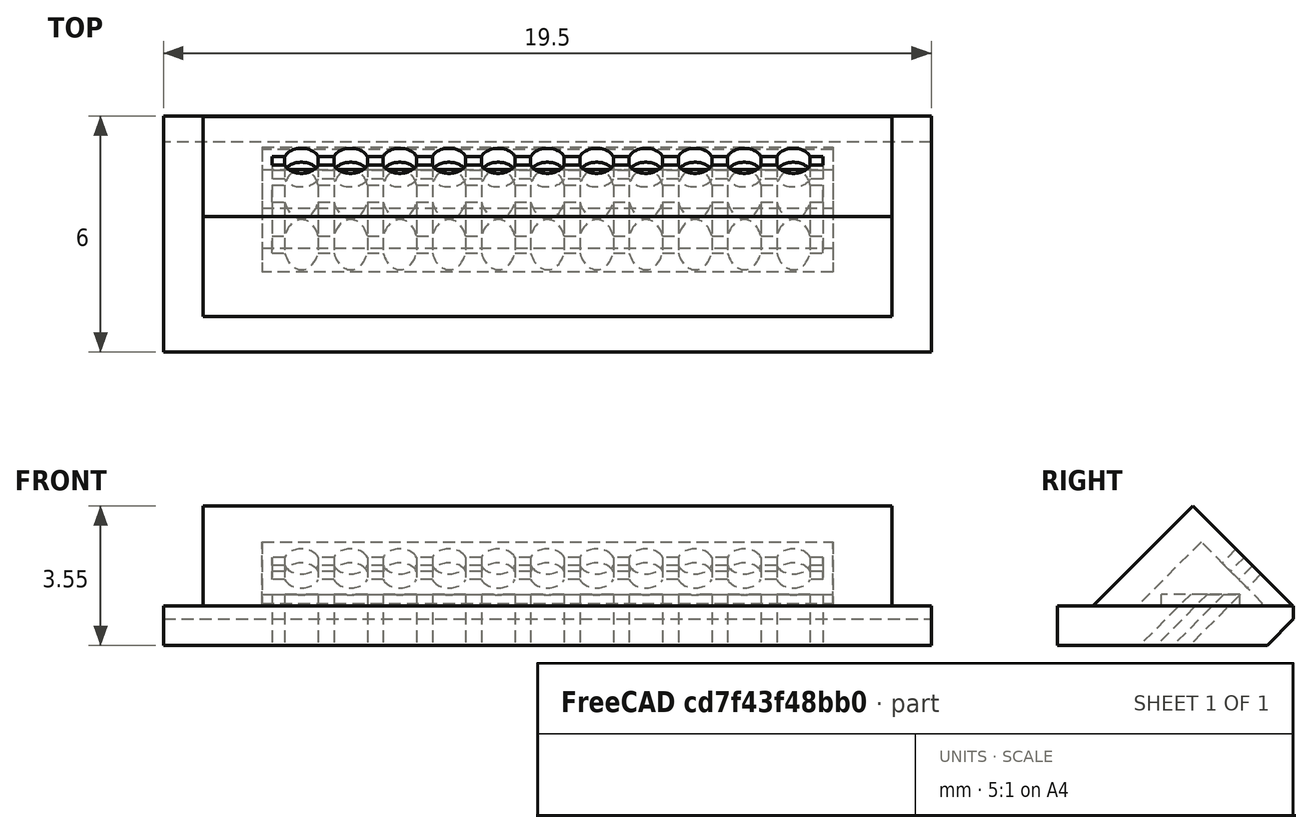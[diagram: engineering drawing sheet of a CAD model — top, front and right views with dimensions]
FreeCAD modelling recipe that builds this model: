
FCSTD DOCUMENT  (FreeCAD 0.18.4R)
Label: CableGasket3
License: All rights reserved
LicenseURL: http://en.wikipedia.org/wiki/All_rights_reserved
objects: Part::Cylinder×22, Part::Box×8, Part::Cut×5, Part::MultiFuse×4, Mesh::Feature×1
note: 39 computed .brp shape members not serialized (recipe doc carries the construction recipe); baked Part::Feature solids carry a one-line shape summary decoded from their .brp

FEATURE [Part::Box] Box001  label="Würfel001"
  AttacherType = Attacher::AttachEngine3D
  Height = 10
  Length = 17.5
  Placement = pos=(-7.5,-2,0) rot=(0,0,1;0rad)
  Width = 4
FEATURE [Part::Box] Box002  label="Würfel002"
  AttacherType = Attacher::AttachEngine3D
  Height = 10
  Length = 20
  Placement = pos=(-10,-3,-0.4) rot=(1,0,0;0.785398rad)
  Width = 14.5
FEATURE [Part::Box] Box003  label="Würfel003"
  AttacherType = Attacher::AttachEngine3D
  Height = 6
  Length = 19.5
  Placement = pos=(-8.5,-2.31,1.7) rot=(-1,0,0;0.785398rad)
  Width = 1
FEATURE [Part::Cylinder] Cylinder009  label="Draht010"
  Angle = 360
  AttacherType = Attacher::AttachEngine3D
  Height = 10
  Radius = 0.45
FEATURE [Part::Cylinder] Cylinder010  label="Draht011"
  Angle = 360
  AttacherType = Attacher::AttachEngine3D
  Height = 10
  Placement = pos=(1.25,0,0) rot=(0,0,1;0rad)
  Radius = 0.45
FEATURE [Part::Cylinder] Cylinder011  label="Draht012"
  Angle = 360
  AttacherType = Attacher::AttachEngine3D
  Height = 10
  Placement = pos=(2.5,0,0) rot=(0,0,1;0rad)
  Radius = 0.45
FEATURE [Part::Cylinder] Cylinder012  label="Draht013"
  Angle = 360
  AttacherType = Attacher::AttachEngine3D
  Height = 10
  Placement = pos=(3.75,0,0) rot=(0,0,1;0rad)
  Radius = 0.45
FEATURE [Part::Cylinder] Cylinder013  label="Draht014"
  Angle = 360
  AttacherType = Attacher::AttachEngine3D
  Height = 10
  Placement = pos=(5,0,0) rot=(0,0,1;0rad)
  Radius = 0.45
FEATURE [Part::Cylinder] Cylinder014  label="Draht015"
  Angle = 360
  AttacherType = Attacher::AttachEngine3D
  Height = 10
  Placement = pos=(-1.25,0,0) rot=(0,0,1;0rad)
  Radius = 0.45
FEATURE [Part::Cylinder] Cylinder015  label="Draht016"
  Angle = 360
  AttacherType = Attacher::AttachEngine3D
  Height = 10
  Placement = pos=(-2.5,0,0) rot=(0,0,1;0rad)
  Radius = 0.45
FEATURE [Part::Cylinder] Cylinder016  label="Draht017"
  Angle = 360
  AttacherType = Attacher::AttachEngine3D
  Height = 10
  Placement = pos=(-3.75,0,0) rot=(0,0,1;0rad)
  Radius = 0.45
FEATURE [Part::Cylinder] Cylinder017  label="Draht018"
  Angle = 360
  AttacherType = Attacher::AttachEngine3D
  Height = 10
  Placement = pos=(-5,0,0) rot=(0,0,1;0rad)
  Radius = 0.45
FEATURE [Part::Box] Box004  label="Würfel004"
  AttacherType = Attacher::AttachEngine3D
  Height = 10
  Length = 14
  Placement = pos=(-5.75,-0.15,0) rot=(0,0,1;0rad)
  Width = 0.3
FEATURE [Part::Box] Box005  label="Würfel005"
  AttacherType = Attacher::AttachEngine3D
  Height = 10
  Length = 14.5
  Placement = pos=(-6,-1,0.5) rot=(0,0,1;0rad)
  Width = 2.2
FEATURE [Part::Cut] Cut
  Base = -> Box001
  Placement = pos=(0,0,1) rot=(0,0,1;0rad)
  Tool = -> Box005
FEATURE [Part::Cut] Cut001
  Base = -> Cut
  Tool = -> Box002
FEATURE [Part::Box] Box006  label="Würfel006"
  AttacherType = Attacher::AttachEngine3D
  Height = 2
  Length = 14.5
  Placement = pos=(-6,-1,2.31) rot=(-1,0,0;0.785398rad)
  Width = 0.8
FEATURE [Part::Cylinder] Cylinder018  label="Draht019"
  Angle = 360
  AttacherType = Attacher::AttachEngine3D
  Height = 10
  Placement = pos=(6.25,0,0) rot=(0,0,1;0rad)
  Radius = 0.45
FEATURE [Part::Cylinder] Cylinder019  label="Draht020"
  Angle = 360
  AttacherType = Attacher::AttachEngine3D
  Height = 10
  Placement = pos=(7.5,0,0) rot=(0,0,1;0rad)
  Radius = 0.45
FEATURE [Part::MultiFuse] Fusion001
  Shapes = -> [Cylinder019,Cylinder009,Cylinder010,Cylinder011,Cylinder012,Cylinder013,Cylinder014,Cylinder015,Cylinder016,Cylinder017,Box004,Cylinder018]
FEATURE [Part::MultiFuse] Fusion002
  Shapes = -> [Box003,Box006]
FEATURE [Part::Cut] Cut003
  Base = -> Fusion002
  Tool = -> Fusion001
FEATURE [Part::Cylinder] Cylinder020  label="Draht021"
  Angle = 360
  AttacherType = Attacher::AttachEngine3D
  Height = 10
  Radius = 0.45
FEATURE [Part::Cylinder] Cylinder021  label="Draht022"
  Angle = 360
  AttacherType = Attacher::AttachEngine3D
  Height = 10
  Placement = pos=(1.25,0,0) rot=(0,0,1;0rad)
  Radius = 0.45
FEATURE [Part::Cylinder] Cylinder022  label="Draht023"
  Angle = 360
  AttacherType = Attacher::AttachEngine3D
  Height = 10
  Placement = pos=(2.5,0,0) rot=(0,0,1;0rad)
  Radius = 0.45
FEATURE [Part::Cylinder] Cylinder023  label="Draht024"
  Angle = 360
  AttacherType = Attacher::AttachEngine3D
  Height = 10
  Placement = pos=(3.75,0,0) rot=(0,0,1;0rad)
  Radius = 0.45
FEATURE [Part::Cylinder] Cylinder024  label="Draht025"
  Angle = 360
  AttacherType = Attacher::AttachEngine3D
  Height = 10
  Placement = pos=(5,0,0) rot=(0,0,1;0rad)
  Radius = 0.45
FEATURE [Part::Cylinder] Cylinder025  label="Draht026"
  Angle = 360
  AttacherType = Attacher::AttachEngine3D
  Height = 10
  Placement = pos=(-1.25,0,0) rot=(0,0,1;0rad)
  Radius = 0.45
FEATURE [Part::Cylinder] Cylinder026  label="Draht027"
  Angle = 360
  AttacherType = Attacher::AttachEngine3D
  Height = 10
  Placement = pos=(-2.5,0,0) rot=(0,0,1;0rad)
  Radius = 0.45
FEATURE [Part::Cylinder] Cylinder027  label="Draht028"
  Angle = 360
  AttacherType = Attacher::AttachEngine3D
  Height = 10
  Placement = pos=(-3.75,0,0) rot=(0,0,1;0rad)
  Radius = 0.45
FEATURE [Part::Cylinder] Cylinder028  label="Draht029"
  Angle = 360
  AttacherType = Attacher::AttachEngine3D
  Height = 10
  Placement = pos=(-5,0,0) rot=(0,0,1;0rad)
  Radius = 0.45
FEATURE [Part::Box] Box007  label="Würfel007"
  AttacherType = Attacher::AttachEngine3D
  Height = 10
  Length = 14
  Placement = pos=(-5.75,-0.15,0) rot=(0,0,1;0rad)
  Width = 0.3
FEATURE [Part::Cylinder] Cylinder029  label="Draht030"
  Angle = 360
  AttacherType = Attacher::AttachEngine3D
  Height = 10
  Placement = pos=(7.5,0,0) rot=(0,0,1;0rad)
  Radius = 0.45
FEATURE [Part::Cylinder] Cylinder030  label="Draht031"
  Angle = 360
  AttacherType = Attacher::AttachEngine3D
  Height = 10
  Placement = pos=(6.25,0,0) rot=(0,0,1;0rad)
  Radius = 0.45
FEATURE [Part::MultiFuse] Fusion003
  Shapes = -> [Cylinder029,Cylinder020,Cylinder021,Cylinder022,Cylinder023,Cylinder024,Cylinder025,Cylinder026,Cylinder027,Cylinder028,Box007,Cylinder030]
FEATURE [Part::Cut] Cut004
  Base = -> Cut001
  Tool = -> Fusion003
FEATURE [Part::MultiFuse] Fusion
  Placement = pos=(0,0,0) rot=(1,0,0;2.35619rad)
  Shapes = -> [Cut004,Cut003]
FEATURE [Part::Box] Box  label="Würfel"
  AttacherType = Attacher::AttachEngine3D
  Height = 3
  Length = 21
  Placement = pos=(-9,-1,-3.6) rot=(1,0,0;-0.785398rad)
  Width = 2
FEATURE [Part::Cut] Cut005
  Base = -> Fusion
  Tool = -> Box
FEATURE [Mesh::Feature] Mesh  label="Cut005 (Meshed)"
